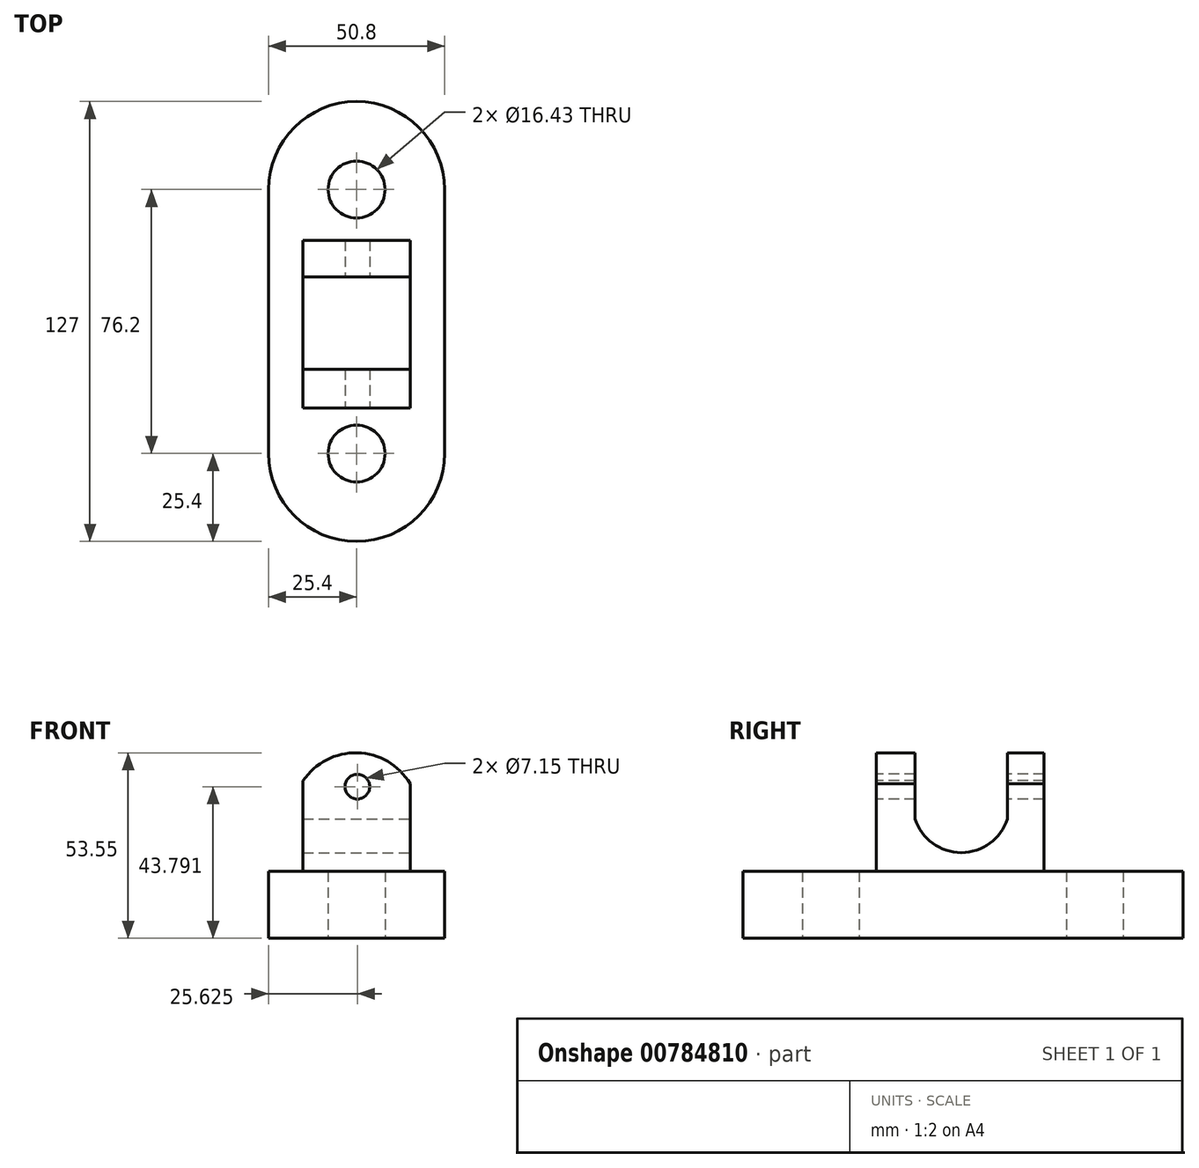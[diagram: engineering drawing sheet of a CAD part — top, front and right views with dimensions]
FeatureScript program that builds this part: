
annotation { "Feature Type Name" : "Feature", "Feature Type Description" : "" }
export const myFeature = defineFeature(function(context is Context, id is Id, definition is map)
    precondition{}
    {
        {
            var Q0;
            Q0=qCreatedBy(makeId("Top.planeOp"),FACE);
            var sketch = newSketch(context, id + "F0", { "sketchPlane" : qUnion([Q0])});
            skCircle(sketch, "E0", {"center": v(0, 38.1) * mm, "radius": 25.4 * mm});
            skCircle(sketch, "E1", {"center": v(0, -38.1) * mm, "radius": 25.4 * mm});
            skLineSegment(sketch, "E2", {"start": v(-25.4, 38.1) * mm, "end": v(-25.4, -38.1) * mm});
            skLineSegment(sketch, "E3", {"start": v(25.4, 38.1) * mm, "end": v(25.4, -38.1) * mm});
            skCircle(sketch, "E4", {"center": v(0, -38.1) * mm, "radius": 8.21 * mm});
            skCircle(sketch, "E5", {"center": v(0, 38.1) * mm, "radius": 8.22 * mm});
            skSolve(sketch);
        }
        {
            var Q0;
            {var subQ0=sQuery(id+"F0.wireOp",EDGE,"E2");Q0=makeQuery(id+"F0.imprint","IMPRINT",FACE,{"disambiguationData":[TD([[makeQuery(id+"F0.imprint","IMPRINT",EDGE,{"derivedFrom":subQ0}),1.0]])]});}
            var Q1;
            Q1=makeQuery(id+"F0.imprint","IMPRINT",FACE,{"disambiguationData":[TD([[makeQuery(id+"F0.imprint","IMPRINT",EDGE,{"derivedFrom":sQuery(id+"F0.wireOp",EDGE,"N1CAscqw-gxDm-tqhV-mefx-K2JMhY2gwXAd")}),-1.0]])]});
            var Q2;
            Q2=makeQuery(id+"F0.imprint","IMPRINT",FACE,{"disambiguationData":[TD([[makeQuery(id+"F0.imprint","IMPRINT",EDGE,{"derivedFrom":sQuery(id+"F0.wireOp",EDGE,"HBleKV9H-s6Cs-CD5E-WN6z-rQkOkA3YoZvv")}),-1.0]])]});
            var Q3;
            Q3=makeQuery(id+"F0.imprint","IMPRINT",FACE,{"disambiguationData":[TD([[makeQuery(id+"F0.imprint","IMPRINT",EDGE,{"derivedFrom":sQuery(id+"F0.wireOp",EDGE,"E4")}),-1.0]])]});
            var Q4;
            Q4=makeQuery(id+"F0.imprint","IMPRINT",FACE,{"disambiguationData":[TD([[makeQuery(id+"F0.imprint","IMPRINT",EDGE,{"derivedFrom":sQuery(id+"F0.wireOp",EDGE,"E5")}),-1.0]])]});
            extrude(context, id + "F1", {"entities" : qUnion([Q0, Q1, Q2, Q3, Q4]), "depth" : 19.3 * mm, "offsetDistance" : 25.4 * mm});
        }
        {
            var Q0;
            Q0=makeQuery(id+"F1.opExtrude","CAP_FACE",FACE,{"disambiguationData":[OSD([sQuery(id+"F0.wireOp",EDGE,"E0"),sQuery(id+"F0.wireOp",EDGE,"E1"),sQuery(id+"F0.wireOp",EDGE,"E2"),sQuery(id+"F0.wireOp",EDGE,"E3"),sQuery(id+"F0.wireOp",EDGE,"E4"),sQuery(id+"F0.wireOp",EDGE,"E5")])],"isStart":false});
            var sketch = newSketch(context, id + "F2", { "sketchPlane" : qUnion([Q0])});
            skLineSegment(sketch, "E6.bottom", {"start": v(-25.4, -24.99) * mm, "end": v(25.4, -24.99) * mm});
            skLineSegment(sketch, "E6.top", {"start": v(-25.4, 23.38) * mm, "end": v(25.4, 23.38) * mm});
            skLineSegment(sketch, "E6.left", {"start": v(-25.4, -24.99) * mm, "end": v(-25.4, 23.38) * mm});
            skLineSegment(sketch, "E6.right", {"start": v(25.4, -24.99) * mm, "end": v(25.4, 23.38) * mm});
            skLineSegment(sketch, "E7", {"start": v(-21.04, -24.99) * mm, "end": v(-21.04, 23.38) * mm});
            skLineSegment(sketch, "E8", {"start": v(21.03, -24.99) * mm, "end": v(21.03, 23.38) * mm});
            skSolve(sketch);
        }
        {
            var Q0;
            {var subQ0=sQuery(id+"F2.wireOp",EDGE,"E7");Q0=makeQuery(id+"F2.imprint","IMPRINT",FACE,{"disambiguationData":[TD([[makeQuery(id+"F2.imprint","IMPRINT",EDGE,{"derivedFrom":subQ0}),-1.0]])]});}
            extrude(context, id + "F3", {"entities" : qUnion([Q0]), "operationType" : NewBodyOperationType.ADD, "depth" : 34.3 * mm, "offsetDistance" : 25.4 * mm});
        }
        {
            var Q0;
            Q0=makeQuery(id+"F3.opExtrude","SWEPT_FACE",FACE,{"disambiguationData":[OSD([sQuery(id+"F2.wireOp",EDGE,"E8")])]});
            extrude(context, id + "F4", {"entities" : qUnion([Q0]), "operationType" : NewBodyOperationType.REMOVE, "oppositeDirection" : true, "depth" : 5.6 * mm, "offsetDistance" : 25.4 * mm});
        }
        {
            var Q0;
            Q0=makeQuery(id+"F3.opExtrude","SWEPT_FACE",FACE,{"disambiguationData":[OSD([sQuery(id+"F2.wireOp",EDGE,"E7")])]});
            extrude(context, id + "F5", {"entities" : qUnion([Q0]), "operationType" : NewBodyOperationType.REMOVE, "oppositeDirection" : true, "depth" : 5.6 * mm, "offsetDistance" : 25.4 * mm});
        }
        {
            var Q0;
            Q0=makeQuery(id+"F3.opExtrude","SWEPT_FACE",FACE,{"disambiguationData":[OSD([sQuery(id+"F2.wireOp",EDGE,"E6.bottom")])]});
            var sketch = newSketch(context, id + "F6", { "sketchPlane" : qUnion([Q0])});
            skArc(sketch, "E9", {"start": v(15.44, 44.67) * mm, "mid": v(0.23, 53.54) * mm, "end": v(-15.45, 45.5) * mm});
            skSolve(sketch);
        }
        {
            var Q0;
            Q0=makeQuery(id+"F4.boolean.opBoolean","COPY",FACE,{"derivedFrom":makeQuery(id+"F4.opExtrude","CAP_FACE",FACE,{"disambiguationData":[OSD([sQuery(id+"F2.wireOp",EDGE,"E8")])],"isStart":false})});
            var sketch = newSketch(context, id + "F7", { "sketchPlane" : qUnion([Q0])});
            skLineSegment(sketch, "E10", {"start": v(-13.81, 53.6) * mm, "end": v(-13.81, 34.45) * mm});
            skLineSegment(sketch, "E11", {"start": v(12.89, 53.6) * mm, "end": v(12.89, 34.45) * mm});
            skArc(sketch, "E12", {"start": v(-13.81, 34.45) * mm, "mid": v(-0.46, 24.74) * mm, "end": v(12.89, 34.45) * mm});
            skSolve(sketch);
        }
        {
            var Q0;
            {var subQ0=sQuery(id+"F7.wireOp",EDGE,"E10");Q0=makeQuery(id+"F7.imprint","IMPRINT",FACE,{"disambiguationData":[TD([[makeQuery(id+"F7.imprint","IMPRINT",EDGE,{"derivedFrom":subQ0}),1.0]])]});}
            extrude(context, id + "F8", {"entities" : qUnion([Q0]), "operationType" : NewBodyOperationType.REMOVE, "oppositeDirection" : true, "depth" : 34.3 * mm, "offsetDistance" : 25.4 * mm});
        }
        {
            var Q0;
            {var subQ0=sQuery(id+"F6.wireOp",EDGE,"E9");Q0=makeQuery(id+"F6.imprint","IMPRINT",FACE,{"disambiguationData":[TD([[makeQuery(id+"F6.imprint","IMPRINT",EDGE,{"derivedFrom":subQ0}),-1.0]])]});}
            extrude(context, id + "F9", {"entities" : qUnion([Q0]), "operationType" : NewBodyOperationType.REMOVE, "oppositeDirection" : true, "depth" : 60.2 * mm, "offsetDistance" : 25.4 * mm});
        }
        {
            var Q0;
            Q0=makeQuery(id+"F3.opExtrude","SWEPT_FACE",FACE,{"disambiguationData":[OSD([sQuery(id+"F2.wireOp",EDGE,"E6.bottom")])]});
            var sketch = newSketch(context, id + "F10", { "sketchPlane" : qUnion([Q0])});
            skCircle(sketch, "E13", {"center": v(0.23, 43.8) * mm, "radius": 3.58 * mm});
            skPoint(sketch, "E13.centerSnap0", {"position": v(0.23, 53.54) * mm});
            skSolve(sketch);
        }
        {
            var Q0;
            Q0=makeQuery(id+"F10.imprint","IMPRINT",FACE,{"disambiguationData":[TD([[makeQuery(id+"F10.imprint","IMPRINT",EDGE,{"derivedFrom":sQuery(id+"F10.wireOp",EDGE,"E13")}),1.0]])]});
            extrude(context, id + "F11", {"entities" : qUnion([Q0]), "operationType" : NewBodyOperationType.REMOVE, "oppositeDirection" : true, "depth" : 65.8 * mm, "offsetDistance" : 25.4 * mm});
        }
    });
